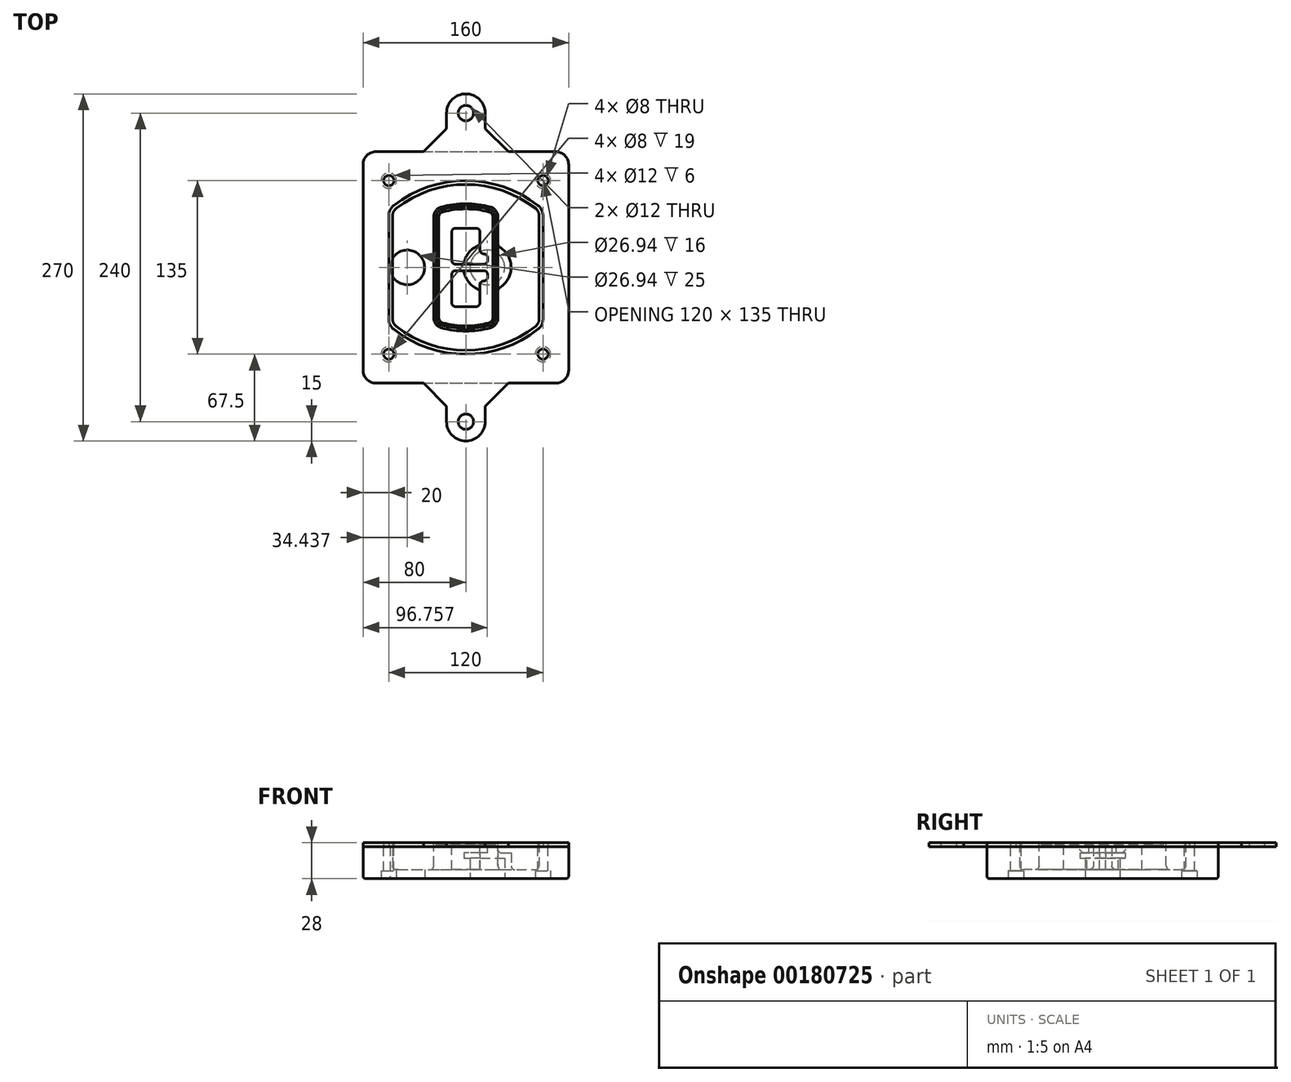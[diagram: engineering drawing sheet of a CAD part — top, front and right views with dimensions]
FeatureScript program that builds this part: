
annotation { "Feature Type Name" : "Feature", "Feature Type Description" : "" }
export const myFeature = defineFeature(function(context is Context, id is Id, definition is map)
    precondition{}
    {
        {
            var Q0;
            Q0=qCreatedBy(makeId("Top.planeOp"),FACE);
            var sketch = newSketch(context, id + "F0", { "sketchPlane" : qUnion([Q0])});
            skPoint(sketch, "E0.rect.middle", {"position": v(0, 0) * mm});
            skLineSegment(sketch, "E1.bottom", {"start": v(-70, -90) * mm, "end": v(70, -90) * mm});
            skLineSegment(sketch, "E1.top", {"start": v(-70, 90) * mm, "end": v(70, 90) * mm});
            skLineSegment(sketch, "E1.left", {"start": v(-80, -80) * mm, "end": v(-80, 80) * mm});
            skLineSegment(sketch, "E1.right", {"start": v(80, -80) * mm, "end": v(80, 80) * mm});
            skLineSegment(sketch, "E2", {"start": v(-80, 90) * mm, "end": v(80, -90) * mm, "construction": true});
            skLineSegment(sketch, "E3", {"start": v(80, 90) * mm, "end": v(-80, -90) * mm, "construction": true});
            skCircle(sketch, "E4", {"center": v(-60, 67.5) * mm, "radius": 4 * mm});
            skCircle(sketch, "E5", {"center": v(60, 67.5) * mm, "radius": 4 * mm});
            skCircle(sketch, "E6", {"center": v(60, -67.5) * mm, "radius": 4 * mm});
            skCircle(sketch, "E7", {"center": v(-60, -67.5) * mm, "radius": 4 * mm});
            skLineSegment(sketch, "E8", {"start": v(-60, 67.5) * mm, "end": v(60, 67.5) * mm, "construction": true});
            skLineSegment(sketch, "E9", {"start": v(60, 67.5) * mm, "end": v(60, -67.5) * mm, "construction": true});
            skLineSegment(sketch, "E10", {"start": v(60, -67.5) * mm, "end": v(-60, -67.5) * mm, "construction": true});
            skLineSegment(sketch, "E11", {"start": v(-60, -67.5) * mm, "end": v(-60, 67.5) * mm, "construction": true});
            skLineSegment(sketch, "E12", {"start": v(-60, 40.3) * mm, "end": v(-60, -40.3) * mm});
            skLineSegment(sketch, "E13", {"start": v(60, 40.3) * mm, "end": v(60, -40.3) * mm});
            skArc(sketch, "E14", {"start": v(56.15, 48.18) * mm, "mid": v(0, 67.5) * mm, "end": v(-56.15, 48.18) * mm});
            skArc(sketch, "E15", {"start": v(-56.15, -48.18) * mm, "mid": v(0, -67.5) * mm, "end": v(56.15, -48.18) * mm});
            skLineSegment(sketch, "E16", {"start": v(-60, 0) * mm, "end": v(60, 0) * mm, "construction": true});
            skPoint(sketch, "E17.visualSharp", {"position": v(-60, -45) * mm});
            skArc(sketch, "E17.filletArc", {"start": v(-60, -40.3) * mm, "mid": v(-58.99, -44.68) * mm, "end": v(-56.15, -48.18) * mm});
            skPoint(sketch, "E18.visualSharp", {"position": v(-60, 45) * mm});
            skArc(sketch, "E18.filletArc", {"start": v(-56.15, 48.18) * mm, "mid": v(-58.99, 44.68) * mm, "end": v(-60, 40.3) * mm});
            skPoint(sketch, "E19.visualSharp", {"position": v(60, 45) * mm});
            skArc(sketch, "E19.filletArc", {"start": v(60, 40.3) * mm, "mid": v(58.99, 44.68) * mm, "end": v(56.15, 48.18) * mm});
            skPoint(sketch, "E20.visualSharp", {"position": v(60, -45) * mm});
            skArc(sketch, "E20.filletArc", {"start": v(56.15, -48.18) * mm, "mid": v(58.99, -44.68) * mm, "end": v(60, -40.3) * mm});
            skPoint(sketch, "E21.visualSharp", {"position": v(-80, 90) * mm});
            skArc(sketch, "E21.filletArc", {"start": v(-70, 90) * mm, "mid": v(-77.07, 87.07) * mm, "end": v(-80, 80) * mm});
            skPoint(sketch, "E22.visualSharp", {"position": v(80, 90) * mm});
            skArc(sketch, "E22.filletArc", {"start": v(80, 80) * mm, "mid": v(77.07, 87.07) * mm, "end": v(70, 90) * mm});
            skPoint(sketch, "E23.visualSharp", {"position": v(80, -90) * mm});
            skArc(sketch, "E23.filletArc", {"start": v(70, -90) * mm, "mid": v(77.07, -87.07) * mm, "end": v(80, -80) * mm});
            skPoint(sketch, "E24.visualSharp", {"position": v(-80, -90) * mm});
            skArc(sketch, "E24.filletArc", {"start": v(-80, -80) * mm, "mid": v(-77.07, -87.07) * mm, "end": v(-70, -90) * mm});
            skArc(sketch, "E25.0", {"start": v(57, 40.3) * mm, "mid": v(56.3, 43.36) * mm, "end": v(54.3, 45.81) * mm});
            skLineSegment(sketch, "E25.1", {"start": v(57, 40.3) * mm, "end": v(57, -40.3) * mm});
            skArc(sketch, "E25.2", {"start": v(54.3, -45.81) * mm, "mid": v(56.3, -43.36) * mm, "end": v(57, -40.3) * mm});
            skArc(sketch, "E25.3", {"start": v(-54.3, -45.81) * mm, "mid": v(0, -64.5) * mm, "end": v(54.3, -45.81) * mm});
            skArc(sketch, "E25.4", {"start": v(-57, -40.3) * mm, "mid": v(-56.3, -43.36) * mm, "end": v(-54.3, -45.81) * mm});
            skArc(sketch, "E25.5", {"start": v(54.3, 45.81) * mm, "mid": v(0, 64.5) * mm, "end": v(-54.3, 45.81) * mm});
            skLineSegment(sketch, "E25.6", {"start": v(-57, 40.3) * mm, "end": v(-57, -40.3) * mm});
            skArc(sketch, "E25.7", {"start": v(-54.3, 45.81) * mm, "mid": v(-56.3, 43.36) * mm, "end": v(-57, 40.3) * mm});
            skArc(sketch, "E26.0", {"start": v(-58.62, 51.33) * mm, "mid": v(-62.58, 46.43) * mm, "end": v(-64, 40.3) * mm});
            skArc(sketch, "E26.1", {"start": v(58.62, 51.33) * mm, "mid": v(0, 71.5) * mm, "end": v(-58.62, 51.33) * mm});
            skArc(sketch, "E26.2", {"start": v(64, 40.3) * mm, "mid": v(62.58, 46.43) * mm, "end": v(58.62, 51.33) * mm});
            skLineSegment(sketch, "E26.3", {"start": v(64, 40.3) * mm, "end": v(64, -40.3) * mm});
            skArc(sketch, "E26.4", {"start": v(58.62, -51.33) * mm, "mid": v(62.58, -46.43) * mm, "end": v(64, -40.3) * mm});
            skLineSegment(sketch, "E26.5", {"start": v(-64, 40.3) * mm, "end": v(-64, -40.3) * mm});
            skArc(sketch, "E26.6", {"start": v(-58.62, -51.33) * mm, "mid": v(0, -71.5) * mm, "end": v(58.62, -51.33) * mm});
            skArc(sketch, "E26.7", {"start": v(-64, -40.3) * mm, "mid": v(-62.58, -46.43) * mm, "end": v(-58.62, -51.33) * mm});
            skSolve(sketch);
        }
        {
            var Q0;
            Q0=makeQuery(id+"F0.imprint","IMPRINT",FACE,{"disambiguationData":[TD([[makeQuery(id+"F0.imprint","IMPRINT",EDGE,{"derivedFrom":sQuery(id+"F0.wireOp",EDGE,"E1.bottom")}),1.0]])]});
            var Q1;
            Q1=makeQuery(id+"F0.imprint","IMPRINT",FACE,{"disambiguationData":[TD([[makeQuery(id+"F0.imprint","IMPRINT",EDGE,{"derivedFrom":sQuery(id+"F0.wireOp",EDGE,"E12")}),1.0]])]});
            var Q2;
            Q2=makeQuery(id+"F0.imprint","IMPRINT",FACE,{"disambiguationData":[TD([[makeQuery(id+"F0.imprint","IMPRINT",EDGE,{"derivedFrom":sQuery(id+"F0.wireOp",EDGE,"E25.0")}),1.0]])]});
            var Q3;
            Q3=makeQuery(id+"F0.imprint","IMPRINT",FACE,{"disambiguationData":[TD([[makeQuery(id+"F0.imprint","IMPRINT",EDGE,{"derivedFrom":sQuery(id+"F0.wireOp",EDGE,"E12")}),-1.0]])]});
            extrude(context, id + "F1", {"entities" : qUnion([Q0, Q1, Q2, Q3]), "oppositeDirection" : true, "depth" : 25 * mm});
        }
        {
            var Q0;
            Q0=makeQuery(id+"F0.imprint","IMPRINT",FACE,{"disambiguationData":[TD([[makeQuery(id+"F0.imprint","IMPRINT",EDGE,{"derivedFrom":sQuery(id+"F0.wireOp",EDGE,"E12")}),1.0]])]});
            extrude(context, id + "F2", {"entities" : qUnion([Q0]), "operationType" : NewBodyOperationType.ADD, "depth" : 3 * mm});
        }
        {
            var Q0;
            Q0=makeQuery(id+"F0.imprint","IMPRINT",FACE,{"disambiguationData":[TD([[makeQuery(id+"F0.imprint","IMPRINT",EDGE,{"derivedFrom":sQuery(id+"F0.wireOp",EDGE,"E25.0")}),1.0]])]});
            extrude(context, id + "F3", {"entities" : qUnion([Q0]), "operationType" : NewBodyOperationType.REMOVE, "oppositeDirection" : true, "depth" : 18 * mm});
        }
        {
            var Q0;
            Q0=makeQuery(id+"F2.opExtrude","CAP_FACE",FACE,{"disambiguationData":[OSD([sQuery(id+"F0.wireOp",EDGE,"E12"),sQuery(id+"F0.wireOp",EDGE,"E13"),sQuery(id+"F0.wireOp",EDGE,"E14"),sQuery(id+"F0.wireOp",EDGE,"E15"),sQuery(id+"F0.wireOp",EDGE,"E17.filletArc"),sQuery(id+"F0.wireOp",EDGE,"E18.filletArc"),sQuery(id+"F0.wireOp",EDGE,"E19.filletArc"),sQuery(id+"F0.wireOp",EDGE,"E20.filletArc"),sQuery(id+"F0.wireOp",EDGE,"E25.0"),sQuery(id+"F0.wireOp",EDGE,"E25.1"),sQuery(id+"F0.wireOp",EDGE,"E25.2"),sQuery(id+"F0.wireOp",EDGE,"E25.3"),sQuery(id+"F0.wireOp",EDGE,"E25.4"),sQuery(id+"F0.wireOp",EDGE,"E25.5"),sQuery(id+"F0.wireOp",EDGE,"E25.6"),sQuery(id+"F0.wireOp",EDGE,"E25.7")])],"isStart":false});
            var sketch = newSketch(context, id + "F4", { "sketchPlane" : qUnion([Q0])});
            skArc(sketch, "E27.0", {"start": v(-19.08, -46.97) * mm, "mid": v(0, -49.5) * mm, "end": v(19.08, -46.97) * mm});
            skArc(sketch, "E28.0", {"start": v(19.08, 46.97) * mm, "mid": v(0, 49.5) * mm, "end": v(-19.08, 46.97) * mm});
            skLineSegment(sketch, "E29", {"start": v(-25, 39.25) * mm, "end": v(-25, -39.25) * mm});
            skLineSegment(sketch, "E30", {"start": v(25, 39.25) * mm, "end": v(25, -39.25) * mm});
            skLineSegment(sketch, "E31", {"start": v(-25, 45.1) * mm, "end": v(25, 45.1) * mm, "construction": true});
            skLineSegment(sketch, "E32", {"start": v(-25, -45.1) * mm, "end": v(25, -45.1) * mm, "construction": true});
            skPoint(sketch, "E33.visualSharp", {"position": v(-25, 45.1) * mm});
            skArc(sketch, "E33.filletArc", {"start": v(-19.08, 46.97) * mm, "mid": v(-23.35, 44.11) * mm, "end": v(-25, 39.25) * mm});
            skPoint(sketch, "E34.visualSharp", {"position": v(25, 45.1) * mm});
            skArc(sketch, "E34.filletArc", {"start": v(25, 39.25) * mm, "mid": v(23.35, 44.11) * mm, "end": v(19.08, 46.97) * mm});
            skPoint(sketch, "E35.visualSharp", {"position": v(25, -45.1) * mm});
            skArc(sketch, "E35.filletArc", {"start": v(19.08, -46.97) * mm, "mid": v(23.35, -44.11) * mm, "end": v(25, -39.25) * mm});
            skPoint(sketch, "E36.visualSharp", {"position": v(-25, -45.1) * mm});
            skArc(sketch, "E36.filletArc", {"start": v(-25, -39.25) * mm, "mid": v(-23.35, -44.11) * mm, "end": v(-19.08, -46.97) * mm});
            skArc(sketch, "E37.0", {"start": v(54.3, 45.81) * mm, "mid": v(0, 64.5) * mm, "end": v(-54.3, 45.81) * mm});
            skArc(sketch, "E37.1", {"start": v(-54.3, 45.81) * mm, "mid": v(-56.3, 43.36) * mm, "end": v(-57, 40.3) * mm});
            skLineSegment(sketch, "E37.2", {"start": v(-57, 40.3) * mm, "end": v(-57, -40.3) * mm});
            skArc(sketch, "E37.3", {"start": v(-57, -40.3) * mm, "mid": v(-56.3, -43.36) * mm, "end": v(-54.3, -45.81) * mm});
            skArc(sketch, "E37.4", {"start": v(-54.3, -45.81) * mm, "mid": v(0, -64.5) * mm, "end": v(54.3, -45.81) * mm});
            skArc(sketch, "E37.5", {"start": v(54.3, -45.81) * mm, "mid": v(56.3, -43.36) * mm, "end": v(57, -40.3) * mm});
            skLineSegment(sketch, "E37.6", {"start": v(57, 40.3) * mm, "end": v(57, -40.3) * mm});
            skArc(sketch, "E37.7", {"start": v(57, 40.3) * mm, "mid": v(56.3, 43.36) * mm, "end": v(54.3, 45.81) * mm});
            skLineSegment(sketch, "E38.0", {"start": v(23, 39.25) * mm, "end": v(23, -39.25) * mm});
            skArc(sketch, "E38.1", {"start": v(18.56, -45.04) * mm, "mid": v(21.76, -42.9) * mm, "end": v(23, -39.25) * mm});
            skArc(sketch, "E38.2", {"start": v(-18.56, -45.04) * mm, "mid": v(0, -47.5) * mm, "end": v(18.56, -45.04) * mm});
            skArc(sketch, "E38.3", {"start": v(-23, -39.25) * mm, "mid": v(-21.76, -42.9) * mm, "end": v(-18.56, -45.04) * mm});
            skLineSegment(sketch, "E38.4", {"start": v(-23, 39.25) * mm, "end": v(-23, -39.25) * mm});
            skArc(sketch, "E38.5", {"start": v(23, 39.25) * mm, "mid": v(21.76, 42.9) * mm, "end": v(18.56, 45.04) * mm});
            skArc(sketch, "E38.6", {"start": v(-18.56, 45.04) * mm, "mid": v(-21.76, 42.9) * mm, "end": v(-23, 39.25) * mm});
            skArc(sketch, "E38.7", {"start": v(18.56, 45.04) * mm, "mid": v(0, 47.5) * mm, "end": v(-18.56, 45.04) * mm});
            skArc(sketch, "E39.0", {"start": v(21, 39.25) * mm, "mid": v(20.18, 41.68) * mm, "end": v(18.04, 43.1) * mm});
            skLineSegment(sketch, "E39.1", {"start": v(21, 39.25) * mm, "end": v(21, -39.25) * mm});
            skArc(sketch, "E39.2", {"start": v(18.04, -43.1) * mm, "mid": v(20.18, -41.68) * mm, "end": v(21, -39.25) * mm});
            skArc(sketch, "E39.3", {"start": v(-18.04, -43.1) * mm, "mid": v(0, -45.5) * mm, "end": v(18.04, -43.1) * mm});
            skArc(sketch, "E39.4", {"start": v(-21, -39.25) * mm, "mid": v(-20.18, -41.68) * mm, "end": v(-18.04, -43.1) * mm});
            skArc(sketch, "E39.5", {"start": v(18.04, 43.1) * mm, "mid": v(0, 45.5) * mm, "end": v(-18.04, 43.1) * mm});
            skLineSegment(sketch, "E39.6", {"start": v(-21, 39.25) * mm, "end": v(-21, -39.25) * mm});
            skArc(sketch, "E39.7", {"start": v(-18.04, 43.1) * mm, "mid": v(-20.18, 41.68) * mm, "end": v(-21, 39.25) * mm});
            skLineSegment(sketch, "E40", {"start": v(-25, 0) * mm, "end": v(25, 0) * mm, "construction": true});
            skLineSegment(sketch, "E41", {"start": v(-11, 5.5) * mm, "end": v(-11, 27.5) * mm});
            skLineSegment(sketch, "E42", {"start": v(-8, 30.5) * mm, "end": v(8, 30.5) * mm});
            skLineSegment(sketch, "E43", {"start": v(11, 27.5) * mm, "end": v(11, 13.5) * mm});
            skLineSegment(sketch, "E44", {"start": v(14, 10.5) * mm, "end": v(14, 10.5) * mm});
            skLineSegment(sketch, "E45", {"start": v(17, 7.5) * mm, "end": v(17, 5.5) * mm});
            skLineSegment(sketch, "E46", {"start": v(14, 2.5) * mm, "end": v(-8, 2.5) * mm});
            skPoint(sketch, "E47.visualSharp", {"position": v(-11, 30.5) * mm});
            skArc(sketch, "E47.filletArc", {"start": v(-8, 30.5) * mm, "mid": v(-10.12, 29.62) * mm, "end": v(-11, 27.5) * mm});
            skPoint(sketch, "E48.visualSharp", {"position": v(11, 30.5) * mm});
            skArc(sketch, "E48.filletArc", {"start": v(11, 27.5) * mm, "mid": v(10.12, 29.62) * mm, "end": v(8, 30.5) * mm});
            skPoint(sketch, "E49.visualSharp", {"position": v(11, 10.5) * mm});
            skArc(sketch, "E49.filletArc", {"start": v(11, 13.5) * mm, "mid": v(11.88, 11.38) * mm, "end": v(14, 10.5) * mm});
            skPoint(sketch, "E50.visualSharp", {"position": v(17, 10.5) * mm});
            skArc(sketch, "E50.filletArc", {"start": v(17, 7.5) * mm, "mid": v(16.12, 9.62) * mm, "end": v(14, 10.5) * mm});
            skPoint(sketch, "E51.visualSharp", {"position": v(17, 2.5) * mm});
            skArc(sketch, "E51.filletArc", {"start": v(14, 2.5) * mm, "mid": v(16.12, 3.38) * mm, "end": v(17, 5.5) * mm});
            skPoint(sketch, "E52.visualSharp", {"position": v(-11, 2.5) * mm});
            skArc(sketch, "E52.filletArc", {"start": v(-11, 5.5) * mm, "mid": v(-10.12, 3.38) * mm, "end": v(-8, 2.5) * mm});
            skLineSegment(sketch, "E53.0.MirrorCS", {"start": v(14, -2.5) * mm, "end": v(-8, -2.5) * mm});
            skArc(sketch, "E54.0.MirrorCS", {"start": v(-11, -5.5) * mm, "mid": v(-10.12, -3.38) * mm, "end": v(-8, -2.5) * mm});
            skLineSegment(sketch, "E55.0.MirrorCS", {"start": v(-11, -5.5) * mm, "end": v(-11, -27.5) * mm});
            skArc(sketch, "E56.0.MirrorCS", {"start": v(-8, -30.5) * mm, "mid": v(-10.12, -29.62) * mm, "end": v(-11, -27.5) * mm});
            skLineSegment(sketch, "E57.0.MirrorCS", {"start": v(-8, -30.5) * mm, "end": v(8, -30.5) * mm});
            skArc(sketch, "E58.0.MirrorCS", {"start": v(11, -27.5) * mm, "mid": v(10.12, -29.62) * mm, "end": v(8, -30.5) * mm});
            skLineSegment(sketch, "E59.0.MirrorCS", {"start": v(11, -27.5) * mm, "end": v(11, -13.5) * mm});
            skArc(sketch, "E60.0.MirrorCS", {"start": v(11, -13.5) * mm, "mid": v(11.88, -11.38) * mm, "end": v(14, -10.5) * mm});
            skArc(sketch, "E61.0.MirrorCS", {"start": v(17, -7.5) * mm, "mid": v(16.12, -9.62) * mm, "end": v(14, -10.5) * mm});
            skLineSegment(sketch, "E62.0.MirrorCS", {"start": v(17, -7.5) * mm, "end": v(17, -5.5) * mm});
            skArc(sketch, "E63.0.MirrorCS", {"start": v(14, -2.5) * mm, "mid": v(16.12, -3.38) * mm, "end": v(17, -5.5) * mm});
            skSolve(sketch);
        }
        {
            var Q0;
            Q0=makeQuery(id+"F4.imprint","IMPRINT",FACE,{"disambiguationData":[TD([[makeQuery(id+"F4.imprint","IMPRINT",EDGE,{"derivedFrom":sQuery(id+"F4.wireOp",EDGE,"E27.0")}),1.0]])]});
            var Q1;
            Q1=makeQuery(id+"F4.imprint","IMPRINT",FACE,{"disambiguationData":[TD([[makeQuery(id+"F4.imprint","IMPRINT",EDGE,{"derivedFrom":sQuery(id+"F4.wireOp",EDGE,"E38.0")}),-1.0]])]});
            var Q2;
            Q2=makeQuery(id+"F4.imprint","IMPRINT",FACE,{"disambiguationData":[TD([[makeQuery(id+"F4.imprint","IMPRINT",EDGE,{"derivedFrom":sQuery(id+"F4.wireOp",EDGE,"E39.0")}),1.0]])]});
            extrude(context, id + "F5", {"entities" : qUnion([Q0, Q1, Q2]), "operationType" : NewBodyOperationType.ADD, "endBound" : BoundingType.UP_TO_NEXT, "oppositeDirection" : true, "depth" : 25 * mm});
        }
        {
            var Q0;
            Q0=makeQuery(id+"F4.imprint","IMPRINT",FACE,{"disambiguationData":[TD([[makeQuery(id+"F4.imprint","IMPRINT",EDGE,{"derivedFrom":sQuery(id+"F4.wireOp",EDGE,"E38.0")}),-1.0]])]});
            extrude(context, id + "F6", {"entities" : qUnion([Q0]), "operationType" : NewBodyOperationType.REMOVE, "oppositeDirection" : true, "depth" : 2 * mm});
        }
        {
            var Q0;
            Q0=makeQuery(id+"F1.opExtrude","CAP_FACE",FACE,{"disambiguationData":[OSD([sQuery(id+"F0.wireOp",EDGE,"E1.bottom"),sQuery(id+"F0.wireOp",EDGE,"E1.top"),sQuery(id+"F0.wireOp",EDGE,"E1.left"),sQuery(id+"F0.wireOp",EDGE,"E1.right"),sQuery(id+"F0.wireOp",EDGE,"E4"),sQuery(id+"F0.wireOp",EDGE,"E5"),sQuery(id+"F0.wireOp",EDGE,"E6"),sQuery(id+"F0.wireOp",EDGE,"E7"),sQuery(id+"F0.wireOp",EDGE,"E21.filletArc"),sQuery(id+"F0.wireOp",EDGE,"E22.filletArc"),sQuery(id+"F0.wireOp",EDGE,"E23.filletArc"),sQuery(id+"F0.wireOp",EDGE,"E24.filletArc")])],"isStart":false});
            var sketch = newSketch(context, id + "F7", { "sketchPlane" : qUnion([Q0])});
            skCircle(sketch, "E64", {"center": v(16.76, 0) * mm, "radius": 13.47 * mm});
            skCircle(sketch, "E65", {"center": v(-45.56, 0) * mm, "radius": 13.47 * mm});
            skLineSegment(sketch, "E66", {"start": v(80, 0) * mm, "end": v(-80, 0) * mm});
            skCircle(sketch, "E67", {"center": v(16.76, 0) * mm, "radius": 18.47 * mm});
            skCircle(sketch, "E68", {"center": v(60, -67.5) * mm, "radius": 6 * mm});
            skCircle(sketch, "E69", {"center": v(-60, -67.5) * mm, "radius": 6 * mm});
            skCircle(sketch, "E70", {"center": v(-60, 67.5) * mm, "radius": 6 * mm});
            skCircle(sketch, "E71", {"center": v(60, 67.5) * mm, "radius": 6 * mm});
            skSolve(sketch);
        }
        {
            var Q0;
            {var subQ1=sQuery(id+"F7.wireOp",EDGE,"E66");var subQ4=sQuery(id+"F7.wireOp",EDGE,"E64");var subQ6=makeQuery(id+"F7.imprint","INTERSECT",VERTEX,{"disambiguationData":[OD(0.0)],"derivedFrom":[subQ4,subQ1]});Q0=makeQuery(id+"F7.imprint","IMPRINT",FACE,{"disambiguationData":[TD([[makeQuery(id+"F7.imprint","IMPRINT",EDGE,{"disambiguationData":[TD([[subQ6,-1.0]])],"derivedFrom":subQ4}),-1.0]])]});}
            var Q1;
            {var subQ0=sQuery(id+"F7.wireOp",EDGE,"E66");var subQ1=sQuery(id+"F7.wireOp",EDGE,"E64");var subQ3=makeQuery(id+"F7.imprint","INTERSECT",VERTEX,{"disambiguationData":[OD(0.0)],"derivedFrom":[subQ1,subQ0]});Q1=makeQuery(id+"F7.imprint","IMPRINT",FACE,{"disambiguationData":[TD([[makeQuery(id+"F7.imprint","IMPRINT",EDGE,{"disambiguationData":[TD([[subQ3,-1.0]])],"derivedFrom":subQ1}),1.0]])]});}
            var Q2;
            {var subQ0=sQuery(id+"F7.wireOp",EDGE,"E66");var subQ1=sQuery(id+"F7.wireOp",EDGE,"E64");var subQ3=makeQuery(id+"F7.imprint","INTERSECT",VERTEX,{"disambiguationData":[OD(0.0)],"derivedFrom":[subQ1,subQ0]});Q2=makeQuery(id+"F7.imprint","IMPRINT",FACE,{"disambiguationData":[TD([[makeQuery(id+"F7.imprint","IMPRINT",EDGE,{"disambiguationData":[TD([[subQ3,1.0]])],"derivedFrom":subQ1}),1.0]])]});}
            var Q3;
            {var subQ1=sQuery(id+"F7.wireOp",EDGE,"E66");var subQ4=sQuery(id+"F7.wireOp",EDGE,"E64");var subQ6=makeQuery(id+"F7.imprint","INTERSECT",VERTEX,{"disambiguationData":[OD(0.0)],"derivedFrom":[subQ4,subQ1]});Q3=makeQuery(id+"F7.imprint","IMPRINT",FACE,{"disambiguationData":[TD([[makeQuery(id+"F7.imprint","IMPRINT",EDGE,{"disambiguationData":[TD([[subQ6,1.0]])],"derivedFrom":subQ4}),-1.0]])]});}
            extrude(context, id + "F8", {"entities" : qUnion([Q0, Q1, Q2, Q3]), "operationType" : NewBodyOperationType.ADD, "oppositeDirection" : true, "depth" : 20 * mm});
        }
        {
            var Q0;
            {var subQ0=sQuery(id+"F7.wireOp",EDGE,"E66");var subQ1=sQuery(id+"F7.wireOp",EDGE,"E64");var subQ3=makeQuery(id+"F7.imprint","INTERSECT",VERTEX,{"disambiguationData":[OD(0.0)],"derivedFrom":[subQ1,subQ0]});Q0=makeQuery(id+"F7.imprint","IMPRINT",FACE,{"disambiguationData":[TD([[makeQuery(id+"F7.imprint","IMPRINT",EDGE,{"disambiguationData":[TD([[subQ3,-1.0]])],"derivedFrom":subQ1}),1.0]])]});}
            var Q1;
            {var subQ0=sQuery(id+"F7.wireOp",EDGE,"E66");var subQ1=sQuery(id+"F7.wireOp",EDGE,"E64");var subQ3=makeQuery(id+"F7.imprint","INTERSECT",VERTEX,{"disambiguationData":[OD(0.0)],"derivedFrom":[subQ1,subQ0]});Q1=makeQuery(id+"F7.imprint","IMPRINT",FACE,{"disambiguationData":[TD([[makeQuery(id+"F7.imprint","IMPRINT",EDGE,{"disambiguationData":[TD([[subQ3,1.0]])],"derivedFrom":subQ1}),1.0]])]});}
            extrude(context, id + "F9", {"entities" : qUnion([Q0, Q1]), "operationType" : NewBodyOperationType.REMOVE, "oppositeDirection" : true, "depth" : 16 * mm});
        }
        {
            var Q0;
            {var subQ0=sQuery(id+"F7.wireOp",EDGE,"E66");var subQ1=sQuery(id+"F7.wireOp",EDGE,"E65");var subQ3=makeQuery(id+"F7.imprint","INTERSECT",VERTEX,{"disambiguationData":[OD(0.0)],"derivedFrom":[subQ1,subQ0]});Q0=makeQuery(id+"F7.imprint","IMPRINT",FACE,{"disambiguationData":[TD([[makeQuery(id+"F7.imprint","IMPRINT",EDGE,{"disambiguationData":[TD([[subQ3,-1.0]])],"derivedFrom":subQ1}),1.0]])]});}
            var Q1;
            {var subQ0=sQuery(id+"F7.wireOp",EDGE,"E66");var subQ1=sQuery(id+"F7.wireOp",EDGE,"E65");var subQ3=makeQuery(id+"F7.imprint","INTERSECT",VERTEX,{"disambiguationData":[OD(0.0)],"derivedFrom":[subQ1,subQ0]});Q1=makeQuery(id+"F7.imprint","IMPRINT",FACE,{"disambiguationData":[TD([[makeQuery(id+"F7.imprint","IMPRINT",EDGE,{"disambiguationData":[TD([[subQ3,1.0]])],"derivedFrom":subQ1}),1.0]])]});}
            extrude(context, id + "F10", {"entities" : qUnion([Q0, Q1]), "operationType" : NewBodyOperationType.REMOVE, "oppositeDirection" : true, "depth" : 25 * mm});
        }
        {
            var Q0;
            Q0=makeQuery(id+"F7.imprint","IMPRINT",FACE,{"disambiguationData":[TD([[makeQuery(id+"F7.imprint","IMPRINT",EDGE,{"derivedFrom":sQuery(id+"F7.wireOp",EDGE,"E68")}),1.0]])]});
            var Q1;
            Q1=makeQuery(id+"F7.imprint","IMPRINT",FACE,{"disambiguationData":[TD([[makeQuery(id+"F7.imprint","IMPRINT",EDGE,{"derivedFrom":makeQuery(id+"F1.opExtrude","CAP_EDGE",EDGE,{"disambiguationData":[OSD([sQuery(id+"F0.wireOp",EDGE,"E5")])],"isStart":false})}),-1.0]])]});
            var Q2;
            Q2=makeQuery(id+"F7.imprint","IMPRINT",FACE,{"disambiguationData":[TD([[makeQuery(id+"F7.imprint","IMPRINT",EDGE,{"derivedFrom":sQuery(id+"F7.wireOp",EDGE,"E69")}),1.0]])]});
            var Q3;
            Q3=makeQuery(id+"F7.imprint","IMPRINT",FACE,{"disambiguationData":[TD([[makeQuery(id+"F7.imprint","IMPRINT",EDGE,{"derivedFrom":makeQuery(id+"F1.opExtrude","CAP_EDGE",EDGE,{"disambiguationData":[OSD([sQuery(id+"F0.wireOp",EDGE,"E4")])],"isStart":false})}),-1.0]])]});
            var Q4;
            Q4=makeQuery(id+"F7.imprint","IMPRINT",FACE,{"disambiguationData":[TD([[makeQuery(id+"F7.imprint","IMPRINT",EDGE,{"derivedFrom":sQuery(id+"F7.wireOp",EDGE,"E70")}),1.0]])]});
            var Q5;
            Q5=makeQuery(id+"F7.imprint","IMPRINT",FACE,{"disambiguationData":[TD([[makeQuery(id+"F7.imprint","IMPRINT",EDGE,{"derivedFrom":makeQuery(id+"F1.opExtrude","CAP_EDGE",EDGE,{"disambiguationData":[OSD([sQuery(id+"F0.wireOp",EDGE,"E7")])],"isStart":false})}),-1.0]])]});
            var Q6;
            Q6=makeQuery(id+"F7.imprint","IMPRINT",FACE,{"disambiguationData":[TD([[makeQuery(id+"F7.imprint","IMPRINT",EDGE,{"derivedFrom":sQuery(id+"F7.wireOp",EDGE,"E71")}),1.0]])]});
            var Q7;
            Q7=makeQuery(id+"F7.imprint","IMPRINT",FACE,{"disambiguationData":[TD([[makeQuery(id+"F7.imprint","IMPRINT",EDGE,{"derivedFrom":makeQuery(id+"F1.opExtrude","CAP_EDGE",EDGE,{"disambiguationData":[OSD([sQuery(id+"F0.wireOp",EDGE,"E6")])],"isStart":false})}),-1.0]])]});
            extrude(context, id + "F11", {"entities" : qUnion([Q0, Q1, Q2, Q3, Q4, Q5, Q6, Q7]), "operationType" : NewBodyOperationType.REMOVE, "oppositeDirection" : true, "depth" : 6 * mm});
        }
        {
            var Q0;
            Q0=makeQuery(id+"F9.boolean.opBoolean","COPY",FACE,{"derivedFrom":makeQuery(id+"F9.opExtrude","CAP_FACE",FACE,{"disambiguationData":[OSD([sQuery(id+"F7.wireOp",EDGE,"E64")])],"isStart":false})});
            var sketch = newSketch(context, id + "F12", { "sketchPlane" : qUnion([Q0])});
            skArc(sketch, "E72.0", {"start": v(11, 17.55) * mm, "mid": v(2.57, 11.82) * mm, "end": v(-1.54, 2.5) * mm});
            skArc(sketch, "E72.1", {"start": v(-1.54, -2.5) * mm, "mid": v(2.57, -11.82) * mm, "end": v(11, -17.55) * mm});
            skLineSegment(sketch, "E73", {"start": v(-1.54, -2.5) * mm, "end": v(14, -2.5) * mm});
            skLineSegment(sketch, "E74.0", {"start": v(14, 2.5) * mm, "end": v(-1.54, 2.5) * mm});
            skArc(sketch, "E74.1", {"start": v(14, 2.5) * mm, "mid": v(16.12, 3.38) * mm, "end": v(17, 5.5) * mm});
            skLineSegment(sketch, "E74.2", {"start": v(17, 7.5) * mm, "end": v(17, 5.5) * mm});
            skArc(sketch, "E74.3", {"start": v(17, 7.5) * mm, "mid": v(16.12, 9.62) * mm, "end": v(14, 10.5) * mm});
            skArc(sketch, "E74.4", {"start": v(11, 13.5) * mm, "mid": v(11.88, 11.38) * mm, "end": v(14, 10.5) * mm});
            skLineSegment(sketch, "E74.5", {"start": v(11, 17.55) * mm, "end": v(11, 13.5) * mm});
            skLineSegment(sketch, "E74.7", {"start": v(14, -2.5) * mm, "end": v(-1.54, -2.5) * mm});
            skArc(sketch, "E74.8", {"start": v(14, -2.5) * mm, "mid": v(16.12, -3.38) * mm, "end": v(17, -5.5) * mm});
            skLineSegment(sketch, "E74.9", {"start": v(17, -7.5) * mm, "end": v(17, -5.5) * mm});
            skArc(sketch, "E74.10", {"start": v(17, -7.5) * mm, "mid": v(16.12, -9.62) * mm, "end": v(14, -10.5) * mm});
            skArc(sketch, "E74.11", {"start": v(11, -13.5) * mm, "mid": v(11.88, -11.38) * mm, "end": v(14, -10.5) * mm});
            skLineSegment(sketch, "E74.12", {"start": v(11, -17.55) * mm, "end": v(11, -13.5) * mm});
            skPoint(sketch, "E75.orphan", {"position": v(11, -27.5) * mm});
            skPoint(sketch, "E76.orphan", {"position": v(-8, -2.5) * mm});
            skPoint(sketch, "E77.orphan", {"position": v(-8, 2.5) * mm});
            skPoint(sketch, "E78.orphan", {"position": v(11, 27.5) * mm});
            skSolve(sketch);
        }
        {
            var Q0;
            {var subQ7=sQuery(id+"F12.wireOp",EDGE,"E72.0");var subQ14=sQuery(id+"F12.wireOp",EDGE,"E72.1");var subQ16=sQuery(id+"F12.wireOp",EDGE,"E74.1");var subQ18=sQuery(id+"F12.wireOp",EDGE,"E74.8");Q0=qUnion([makeQuery(id+"F12.imprint","IMPRINT",FACE,{"disambiguationData":[TD([[makeQuery(id+"F12.imprint","IMPRINT",EDGE,{"derivedFrom":subQ7}),1.0]])]}),makeQuery(id+"F12.imprint","IMPRINT",FACE,{"disambiguationData":[TD([[makeQuery(id+"F12.imprint","IMPRINT",EDGE,{"derivedFrom":subQ14}),1.0]])]}),makeQuery(id+"F12.imprint","IMPRINT",FACE,{"disambiguationData":[TD([[makeQuery(id+"F12.imprint","IMPRINT",EDGE,{"derivedFrom":subQ16}),1.0]])]}),makeQuery(id+"F12.imprint","IMPRINT",FACE,{"disambiguationData":[TD([[makeQuery(id+"F12.imprint","IMPRINT",EDGE,{"derivedFrom":subQ18}),-1.0]])]})]);}
            var Q1;
            Q1=makeQuery(id+"F5.boolean.opBoolean","SPLIT",FACE,{"disambiguationData":[TD([makeQuery(id+"F5.opExtrude","SWEPT_FACE",FACE,{"disambiguationData":[OSD([sQuery(id+"F4.wireOp",EDGE,"E41")])]})])],"derivedFrom":makeQuery(id+"F3.boolean.opBoolean","COPY",FACE,{"derivedFrom":makeQuery(id+"F3.opExtrude","CAP_FACE",FACE,{"disambiguationData":[OSD([sQuery(id+"F0.wireOp",EDGE,"E25.0"),sQuery(id+"F0.wireOp",EDGE,"E25.1"),sQuery(id+"F0.wireOp",EDGE,"E25.2"),sQuery(id+"F0.wireOp",EDGE,"E25.3"),sQuery(id+"F0.wireOp",EDGE,"E25.4"),sQuery(id+"F0.wireOp",EDGE,"E25.5"),sQuery(id+"F0.wireOp",EDGE,"E25.6"),sQuery(id+"F0.wireOp",EDGE,"E25.7")])],"isStart":false})})});
            extrude(context, id + "F13", {"entities" : qUnion([Q0]), "operationType" : NewBodyOperationType.REMOVE, "endBound" : BoundingType.UP_TO_SURFACE, "endBoundEntityFace" : qUnion([Q1]), "depth" : 25 * mm});
        }
        {
            var Q0;
            Q0=makeQuery(id+"F3.boolean.opBoolean","COPY",EDGE,{"derivedFrom":makeQuery(id+"F3.opExtrude","CAP_EDGE",EDGE,{"disambiguationData":[OSD([sQuery(id+"F0.wireOp",EDGE,"E25.6")])],"isStart":false})});
            var Q1;
            Q1=makeQuery(id+"F8.boolean.opBoolean","INTERSECT",EDGE,{"derivedFrom":[makeQuery(id+"F5.opExtrude","SWEPT_FACE",FACE,{"disambiguationData":[OSD([sQuery(id+"F4.wireOp",EDGE,"E30")])]}),makeQuery(id+"F8.opExtrude","CAP_FACE",FACE,{"disambiguationData":[OSD([sQuery(id+"F7.wireOp",EDGE,"E67")])],"isStart":false})]});
            var Q2;
            Q2=makeQuery(id+"F8.boolean.opBoolean","INTERSECT",EDGE,{"disambiguationData":[OD(1.0)],"derivedFrom":[makeQuery(id+"F5.opExtrude","SWEPT_FACE",FACE,{"disambiguationData":[OSD([sQuery(id+"F4.wireOp",EDGE,"E30")])]}),makeQuery(id+"F8.opExtrude","SWEPT_FACE",FACE,{"disambiguationData":[OSD([sQuery(id+"F7.wireOp",EDGE,"E67")])]})]});
            var Q3;
            {var subQ0=sQuery(id+"F4.wireOp",EDGE,"E30");Q3=makeQuery(id+"F8.boolean.opBoolean","SPLIT",EDGE,{"disambiguationData":[TD([makeQuery(id+"F5.opExtrude","SWEPT_FACE",FACE,{"disambiguationData":[OSD([sQuery(id+"F4.wireOp",EDGE,"E35.filletArc")])]})])],"derivedFrom":makeQuery(id+"F5.opExtrude","CAP_EDGE",EDGE,{"disambiguationData":[OSD([subQ0])],"isStart":false})});}
            var Q4;
            {var subQ0=sQuery(id+"F0.wireOp",EDGE,"E25.7");var subQ1=sQuery(id+"F0.wireOp",EDGE,"E25.1");var subQ2=sQuery(id+"F0.wireOp",EDGE,"E25.6");var subQ3=sQuery(id+"F0.wireOp",EDGE,"E25.5");var subQ4=sQuery(id+"F0.wireOp",EDGE,"E25.4");var subQ5=sQuery(id+"F0.wireOp",EDGE,"E25.0");var subQ6=sQuery(id+"F0.wireOp",EDGE,"E25.2");var subQ7=sQuery(id+"F0.wireOp",EDGE,"E25.3");Q4=makeQuery(id+"F8.boolean.opBoolean","INTERSECT",EDGE,{"derivedFrom":[makeQuery(id+"F5.boolean.opBoolean","SPLIT",FACE,{"disambiguationData":[TD([makeQuery(id+"F2.opExtrude","SWEPT_FACE",FACE,{"disambiguationData":[OSD([subQ5])]})])],"derivedFrom":makeQuery(id+"F3.boolean.opBoolean","COPY",FACE,{"derivedFrom":makeQuery(id+"F3.opExtrude","CAP_FACE",FACE,{"disambiguationData":[OSD([subQ5,subQ1,subQ6,subQ7,subQ4,subQ3,subQ2,subQ0])],"isStart":false})})}),makeQuery(id+"F8.opExtrude","SWEPT_FACE",FACE,{"disambiguationData":[OSD([sQuery(id+"F7.wireOp",EDGE,"E67")])]})]});}
            var Q5;
            Q5=makeQuery(id+"F8.boolean.opBoolean","INTERSECT",EDGE,{"disambiguationData":[OD(0.0)],"derivedFrom":[makeQuery(id+"F5.opExtrude","SWEPT_FACE",FACE,{"disambiguationData":[OSD([sQuery(id+"F4.wireOp",EDGE,"E30")])]}),makeQuery(id+"F8.opExtrude","SWEPT_FACE",FACE,{"disambiguationData":[OSD([sQuery(id+"F7.wireOp",EDGE,"E67")])]})]});
            fillet(context, id + "F14", {"entities" : qUnion([Q0, Q1, Q2, Q3, Q4, Q5]), "radius" : 3 * mm, "tangentPropagation" : true, "allowEdgeOverflow" : false});
        }
        {
            var Q0;
            Q0=makeQuery(id+"F1.opExtrude","CAP_EDGE",EDGE,{"disambiguationData":[OSD([sQuery(id+"F0.wireOp",EDGE,"E1.bottom")])],"isStart":false});
            fillet(context, id + "F15", {"entities" : qUnion([Q0]), "radius" : 2 * mm, "tangentPropagation" : true, "allowEdgeOverflow" : false});
        }
        {
            var Q0;
            {var subQ0=sQuery(id+"F0.wireOp",EDGE,"E22.filletArc");var subQ1=sQuery(id+"F0.wireOp",EDGE,"E7");var subQ2=sQuery(id+"F0.wireOp",EDGE,"E6");var subQ3=sQuery(id+"F0.wireOp",EDGE,"E5");var subQ4=sQuery(id+"F0.wireOp",EDGE,"E4");var subQ5=sQuery(id+"F0.wireOp",EDGE,"E1.bottom");var subQ6=sQuery(id+"F0.wireOp",EDGE,"E21.filletArc");var subQ7=sQuery(id+"F0.wireOp",EDGE,"E1.top");var subQ8=sQuery(id+"F0.wireOp",EDGE,"E1.left");var subQ9=sQuery(id+"F0.wireOp",EDGE,"E1.right");var subQ10=sQuery(id+"F0.wireOp",EDGE,"E23.filletArc");var subQ11=sQuery(id+"F0.wireOp",EDGE,"E24.filletArc");Q0=makeQuery(id+"F2.boolean.opBoolean","SPLIT",FACE,{"disambiguationData":[TD([makeQuery(id+"F1.opExtrude","SWEPT_FACE",FACE,{"disambiguationData":[OSD([subQ5])]})])],"derivedFrom":makeQuery(id+"F1.opExtrude","CAP_FACE",FACE,{"disambiguationData":[OSD([subQ5,subQ7,subQ8,subQ9,subQ4,subQ3,subQ2,subQ1,subQ6,subQ0,subQ10,subQ11])],"isStart":true})});}
            var sketch = newSketch(context, id + "F16", { "sketchPlane" : qUnion([Q0])});
            skArc(sketch, "E79.0.0", {"start": v(-80, -80) * mm, "mid": v(-77.07, -87.07) * mm, "end": v(-70, -90) * mm});
            skLineSegment(sketch, "E79.0.1", {"start": v(-70, -90) * mm, "end": v(70, -90) * mm});
            skArc(sketch, "E79.0.2", {"start": v(70, -90) * mm, "mid": v(77.07, -87.07) * mm, "end": v(80, -80) * mm});
            skLineSegment(sketch, "E79.0.3", {"start": v(80, -80) * mm, "end": v(80, 80) * mm});
            skArc(sketch, "E79.0.4", {"start": v(80, 80) * mm, "mid": v(77.07, 87.07) * mm, "end": v(70, 90) * mm});
            skLineSegment(sketch, "E79.0.5", {"start": v(70, 90) * mm, "end": v(-70, 90) * mm});
            skArc(sketch, "E79.0.6", {"start": v(-70, 90) * mm, "mid": v(-77.07, 87.07) * mm, "end": v(-80, 80) * mm});
            skLineSegment(sketch, "E79.0.7", {"start": v(-80, 80) * mm, "end": v(-80, -80) * mm});
            skCircle(sketch, "E80.0", {"center": v(-60, 67.5) * mm, "radius": 4 * mm});
            skCircle(sketch, "E81.0", {"center": v(60, 67.5) * mm, "radius": 4 * mm});
            skCircle(sketch, "E82.0", {"center": v(60, -67.5) * mm, "radius": 4 * mm});
            skCircle(sketch, "E83.0", {"center": v(-60, -67.5) * mm, "radius": 4 * mm});
            skLineSegment(sketch, "E84", {"start": v(0, 90) * mm, "end": v(0, 120) * mm, "construction": true});
            skPoint(sketch, "E84.endSnap0", {"position": v(0, 90) * mm});
            skCircle(sketch, "E85", {"center": v(0, 120) * mm, "radius": 6 * mm});
            skArc(sketch, "E86", {"start": v(15, 120) * mm, "mid": v(0, 135) * mm, "end": v(-15, 120) * mm});
            skLineSegment(sketch, "E87", {"start": v(-15, 120) * mm, "end": v(-15, 108) * mm});
            skLineSegment(sketch, "E88", {"start": v(-15, 108) * mm, "end": v(-33, 90) * mm});
            skLineSegment(sketch, "E89.MirrorCS", {"start": v(15, 108) * mm, "end": v(33, 90) * mm});
            skLineSegment(sketch, "E90.MirrorCS", {"start": v(15, 120) * mm, "end": v(15, 108) * mm});
            skLineSegment(sketch, "E91", {"start": v(-80, 0) * mm, "end": v(80, 0) * mm, "construction": true});
            skPoint(sketch, "E92.MirrorP", {"position": v(0, -90) * mm});
            skLineSegment(sketch, "E93.MirrorCS", {"start": v(-15, -120) * mm, "end": v(-15, -108) * mm});
            skLineSegment(sketch, "E94.MirrorCS", {"start": v(-15, -108) * mm, "end": v(-33, -90) * mm});
            skLineSegment(sketch, "E95.MirrorCS", {"start": v(15, -108) * mm, "end": v(33, -90) * mm});
            skLineSegment(sketch, "E96.MirrorCS", {"start": v(15, -120) * mm, "end": v(15, -108) * mm});
            skArc(sketch, "E97.MirrorCS", {"start": v(15, -120) * mm, "mid": v(0, -135) * mm, "end": v(-15, -120) * mm});
            skCircle(sketch, "E98.MirrorC", {"center": v(0, -120) * mm, "radius": 6 * mm});
            skSolve(sketch);
        }
        {
            var Q0;
            Q0=makeQuery(id+"F16.imprint","IMPRINT",FACE,{"disambiguationData":[TD([[makeQuery(id+"F16.imprint","IMPRINT",EDGE,{"derivedFrom":sQuery(id+"F16.wireOp",EDGE,"E93.MirrorCS")}),-1.0]])]});
            var Q1;
            Q1=makeQuery(id+"F16.imprint","IMPRINT",FACE,{"disambiguationData":[TD([[makeQuery(id+"F16.imprint","IMPRINT",EDGE,{"derivedFrom":sQuery(id+"F16.wireOp",EDGE,"E85")}),-1.0]])]});
            var Q2;
            {var subQ8=sQuery(id+"F16.wireOp",EDGE,"E79.0.0");Q2=makeQuery(id+"F16.imprint","IMPRINT",FACE,{"disambiguationData":[TD([[makeQuery(id+"F16.imprint","IMPRINT",EDGE,{"derivedFrom":subQ8}),1.0]])]});}
            var Q3;
            Q3=makeQuery(id+"F2.opExtrude","CAP_FACE",FACE,{"disambiguationData":[OSD([sQuery(id+"F0.wireOp",EDGE,"E12"),sQuery(id+"F0.wireOp",EDGE,"E13"),sQuery(id+"F0.wireOp",EDGE,"E14"),sQuery(id+"F0.wireOp",EDGE,"E15"),sQuery(id+"F0.wireOp",EDGE,"E17.filletArc"),sQuery(id+"F0.wireOp",EDGE,"E18.filletArc"),sQuery(id+"F0.wireOp",EDGE,"E19.filletArc"),sQuery(id+"F0.wireOp",EDGE,"E20.filletArc"),sQuery(id+"F0.wireOp",EDGE,"E25.0"),sQuery(id+"F0.wireOp",EDGE,"E25.1"),sQuery(id+"F0.wireOp",EDGE,"E25.2"),sQuery(id+"F0.wireOp",EDGE,"E25.3"),sQuery(id+"F0.wireOp",EDGE,"E25.4"),sQuery(id+"F0.wireOp",EDGE,"E25.5"),sQuery(id+"F0.wireOp",EDGE,"E25.6"),sQuery(id+"F0.wireOp",EDGE,"E25.7")])],"isStart":false});
            extrude(context, id + "F17", {"entities" : qUnion([Q0, Q1, Q2]), "endBound" : BoundingType.UP_TO_SURFACE, "endBoundEntityFace" : qUnion([Q3]), "depth" : 92 * mm});
        }
    });
